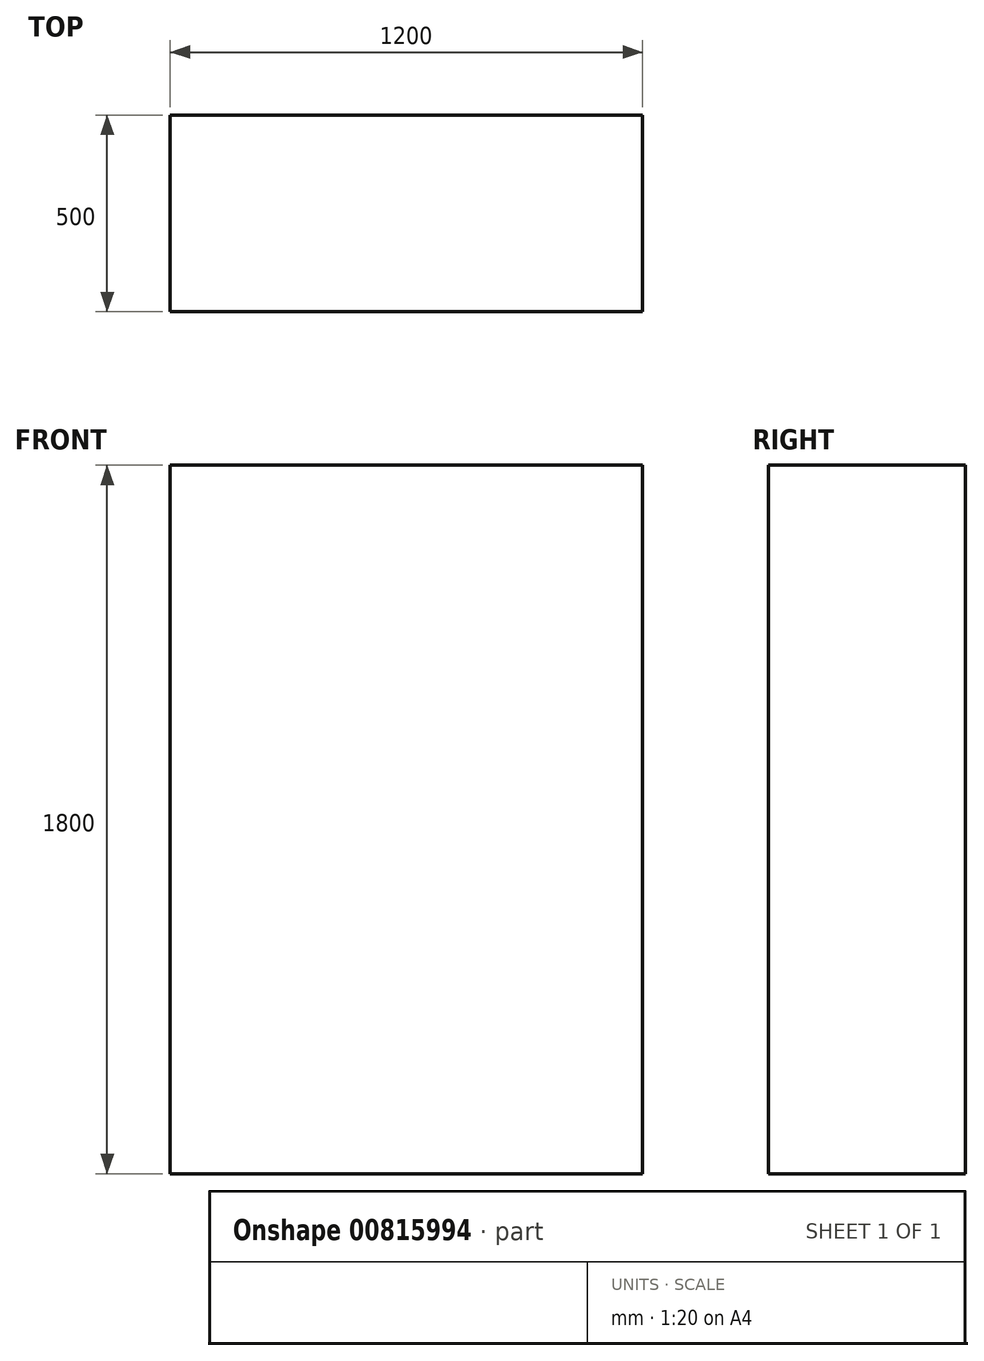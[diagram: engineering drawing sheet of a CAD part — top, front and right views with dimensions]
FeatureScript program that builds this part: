
annotation { "Feature Type Name" : "Feature", "Feature Type Description" : "" }
export const myFeature = defineFeature(function(context is Context, id is Id, definition is map)
    precondition{}
    {
        {
            var Q0;
            Q0=qCreatedBy(makeId("Top.planeOp"),FACE);
            var sketch = newSketch(context, id + "F0", { "sketchPlane" : qUnion([Q0])});
            skLineSegment(sketch, "E0.bottom", {"start": v(-600, 250) * mm, "end": v(600, 250) * mm});
            skLineSegment(sketch, "E0.top", {"start": v(-600, -250) * mm, "end": v(600, -250) * mm});
            skLineSegment(sketch, "E0.left", {"start": v(-600, 250) * mm, "end": v(-600, -250) * mm});
            skLineSegment(sketch, "E0.right", {"start": v(600, 250) * mm, "end": v(600, -250) * mm});
            skPoint(sketch, "E0.middle", {"position": v(0, 0) * mm});
            skSolve(sketch);
        }
        {
            var Q0;
            Q0 = qSketchRegion(id + "F0", true);
            extrude(context, id + "F1", {"entities" : qUnion([Q0]), "depth" : 1800 * mm, "offsetDistance" : 25.4 * mm});
        }
    });
